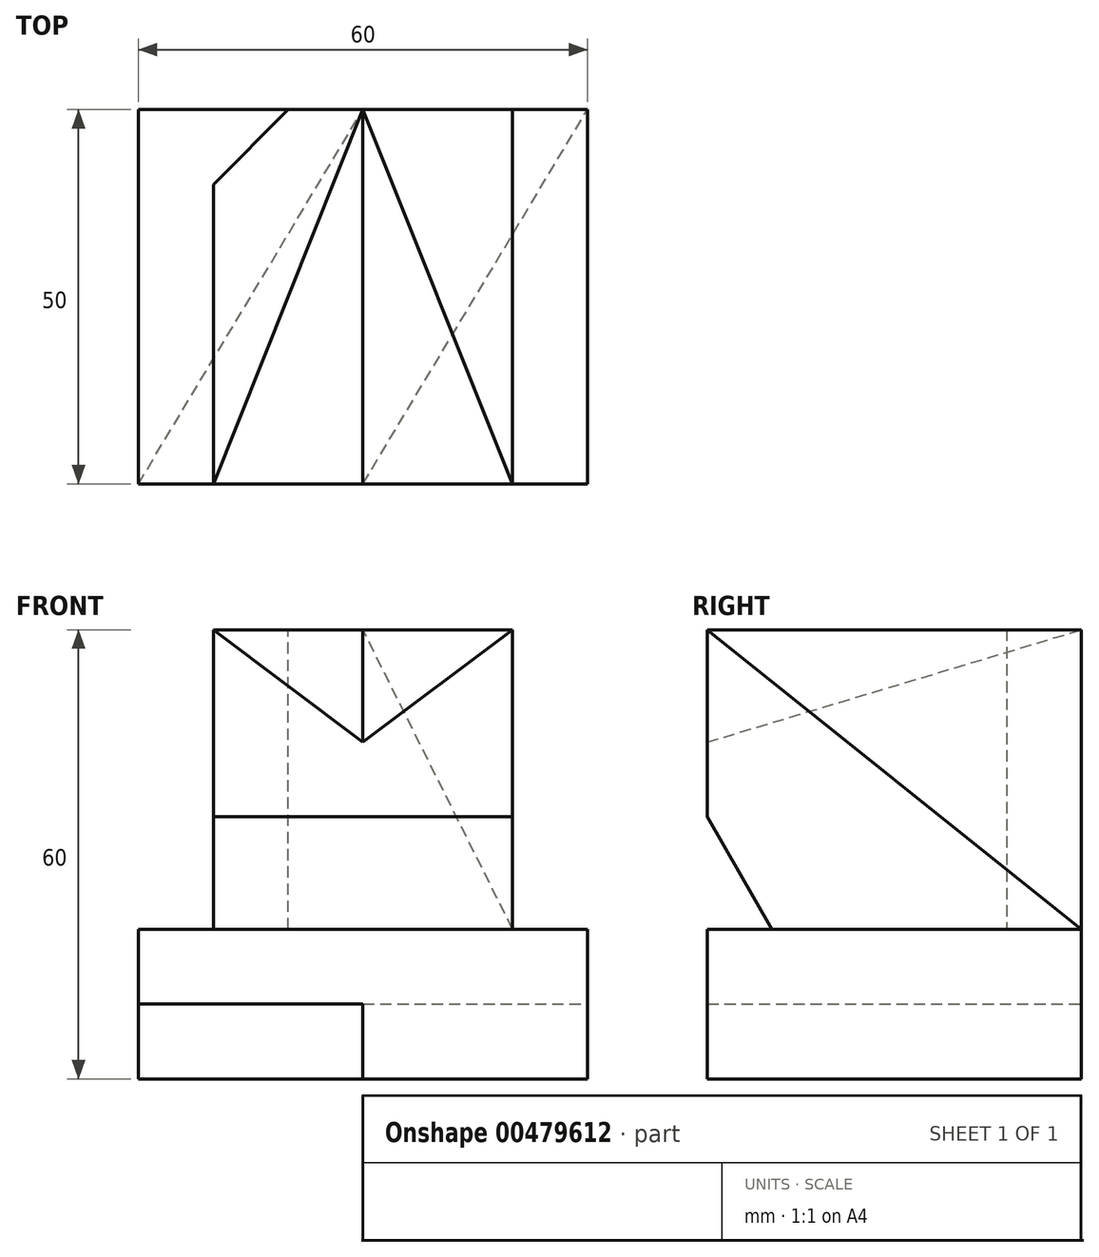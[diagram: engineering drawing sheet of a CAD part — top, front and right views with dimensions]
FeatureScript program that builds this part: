
annotation { "Feature Type Name" : "Feature", "Feature Type Description" : "" }
export const myFeature = defineFeature(function(context is Context, id is Id, definition is map)
    precondition{}
    {
        {
            var Q0;
            Q0=qCreatedBy(makeId("Top.planeOp"),FACE);
            var sketch = newSketch(context, id + "F0", { "sketchPlane" : qUnion([Q0])});
            skLineSegment(sketch, "E0.bottom", {"start": v(0, 0) * mm, "end": v(60, 0) * mm});
            skLineSegment(sketch, "E0.top", {"start": v(0, 50) * mm, "end": v(60, 50) * mm});
            skLineSegment(sketch, "E0.left", {"start": v(0, 0) * mm, "end": v(0, 50) * mm});
            skLineSegment(sketch, "E0.right", {"start": v(60, 0) * mm, "end": v(60, 50) * mm});
            skSolve(sketch);
        }
        {
            var Q0;
            Q0 = qSketchRegion(id + "F0", true);
            extrude(context, id + "F1", {"entities" : qUnion([Q0]), "depth" : 60 * mm});
        }
        {
            var Q0;
            Q0=makeQuery(id+"F1.opExtrude","SWEPT_FACE",FACE,{"disambiguationData":[OSD([sQuery(id+"F0.wireOp",EDGE,"E0.bottom")])]});
            var sketch = newSketch(context, id + "F2", { "sketchPlane" : qUnion([Q0])});
            skLineSegment(sketch, "E1.bottom", {"start": v(0, 60) * mm, "end": v(10, 60) * mm});
            skLineSegment(sketch, "E1.top", {"start": v(0, 20) * mm, "end": v(10, 20) * mm});
            skLineSegment(sketch, "E1.left", {"start": v(0, 60) * mm, "end": v(0, 20) * mm});
            skLineSegment(sketch, "E1.right", {"start": v(10, 60) * mm, "end": v(10, 20) * mm});
            skSolve(sketch);
        }
        {
            var Q0;
            Q0=makeQuery(id+"F2.imprint","IMPRINT",FACE,{"disambiguationData":[TD([[makeQuery(id+"F2.imprint","IMPRINT",EDGE,{"derivedFrom":sQuery(id+"F2.wireOp",EDGE,"E1.bottom")}),-1.0]])]});
            extrude(context, id + "F3", {"entities" : qUnion([Q0]), "operationType" : NewBodyOperationType.REMOVE, "endBound" : BoundingType.THROUGH_ALL, "oppositeDirection" : true, "depth" : 25 * mm, "offsetDistance" : 25 * mm});
        }
        {
            var Q0;
            Q0=makeQuery(id+"F1.opExtrude","SWEPT_FACE",FACE,{"disambiguationData":[OSD([sQuery(id+"F0.wireOp",EDGE,"E0.bottom")])]});
            var sketch = newSketch(context, id + "F4", { "sketchPlane" : qUnion([Q0])});
            skLineSegment(sketch, "E2.bottom", {"start": v(60, 60) * mm, "end": v(50, 60) * mm});
            skLineSegment(sketch, "E2.top", {"start": v(60, 20) * mm, "end": v(50, 20) * mm});
            skLineSegment(sketch, "E2.left", {"start": v(60, 60) * mm, "end": v(60, 20) * mm});
            skLineSegment(sketch, "E2.right", {"start": v(50, 60) * mm, "end": v(50, 20) * mm});
            skSolve(sketch);
        }
        {
            var Q0;
            Q0=makeQuery(id+"F4.imprint","IMPRINT",FACE,{"disambiguationData":[TD([[makeQuery(id+"F4.imprint","IMPRINT",EDGE,{"derivedFrom":sQuery(id+"F4.wireOp",EDGE,"E2.bottom")}),-1.0]])]});
            extrude(context, id + "F5", {"entities" : qUnion([Q0]), "operationType" : NewBodyOperationType.REMOVE, "endBound" : BoundingType.THROUGH_ALL, "oppositeDirection" : true, "depth" : 25 * mm, "offsetDistance" : 25 * mm});
        }
        {
            var Q0;
            Q0=makeQuery(id+"F1.opExtrude","CAP_FACE",FACE,{"disambiguationData":[OSD([sQuery(id+"F0.wireOp",EDGE,"E0.bottom"),sQuery(id+"F0.wireOp",EDGE,"E0.top"),sQuery(id+"F0.wireOp",EDGE,"E0.left"),sQuery(id+"F0.wireOp",EDGE,"E0.right")])],"isStart":true});
            var sketch = newSketch(context, id + "F6", { "sketchPlane" : qUnion([Q0])});
            skLineSegment(sketch, "E3", {"start": v(0, 0) * mm, "end": v(30, -50) * mm});
            skLineSegment(sketch, "E4", {"start": v(30, 0) * mm, "end": v(60, -50) * mm});
            skSolve(sketch);
        }
        {
            var Q0;
            {var subQ0=sQuery(id+"F6.wireOp",EDGE,"E3");Q0=makeQuery(id+"F6.imprint","IMPRINT",FACE,{"disambiguationData":[TD([[makeQuery(id+"F6.imprint","IMPRINT",EDGE,{"derivedFrom":subQ0}),1.0]])]});}
            extrude(context, id + "F7", {"entities" : qUnion([Q0]), "operationType" : NewBodyOperationType.REMOVE, "oppositeDirection" : true, "depth" : 10 * mm, "offsetDistance" : 25 * mm});
        }
        {
            var Q0;
            Q0=makeQuery(id+"F3.boolean.opBoolean","INTERSECT",EDGE,{"derivedFrom":[makeQuery(id+"F1.opExtrude","SWEPT_FACE",FACE,{"disambiguationData":[OSD([sQuery(id+"F0.wireOp",EDGE,"E0.top")])]}),makeQuery(id+"F3.opExtrude","SWEPT_FACE",FACE,{"disambiguationData":[OSD([sQuery(id+"F2.wireOp",EDGE,"E1.right")])]})]});
            chamfer(context, id + "F8", {"entities" : qUnion([Q0]), "width" : 10 * mm, "tangentPropagation" : true});
        }
        {
            var Q0;
            Q0=makeQuery(id+"F5.boolean.opBoolean","COPY",FACE,{"derivedFrom":makeQuery(id+"F5.opExtrude","SWEPT_FACE",FACE,{"disambiguationData":[OSD([sQuery(id+"F4.wireOp",EDGE,"E2.right")])]})});
            var sketch = newSketch(context, id + "F9", { "sketchPlane" : qUnion([Q0])});
            skLineSegment(sketch, "E5", {"start": v(0, 35) * mm, "end": v(8.66, 20) * mm});
            skSolve(sketch);
        }
        {
            var Q0;
            {var subQ0=sQuery(id+"F9.wireOp",EDGE,"E5");Q0=makeQuery(id+"F9.imprint","IMPRINT",FACE,{"disambiguationData":[TD([[makeQuery(id+"F9.imprint","IMPRINT",EDGE,{"derivedFrom":subQ0}),-1.0]])]});}
            extrude(context, id + "F10", {"entities" : qUnion([Q0]), "operationType" : NewBodyOperationType.REMOVE, "endBound" : BoundingType.THROUGH_ALL, "oppositeDirection" : true, "depth" : 25 * mm, "offsetDistance" : 25 * mm});
        }
        {
            var Q0;
            {var subQ0=sQuery(id+"F0.wireOp",EDGE,"E0.bottom");Q0=makeQuery(id+"F10.boolean.opBoolean","SPLIT",FACE,{"disambiguationData":[TD([makeQuery(id+"F3.boolean.opBoolean","COPY",FACE,{"derivedFrom":makeQuery(id+"F3.opExtrude","SWEPT_FACE",FACE,{"disambiguationData":[OSD([sQuery(id+"F2.wireOp",EDGE,"E1.right")])]})})])],"derivedFrom":makeQuery(id+"F1.opExtrude","SWEPT_FACE",FACE,{"disambiguationData":[OSD([subQ0])]})});}
            var sketch = newSketch(context, id + "F11", { "sketchPlane" : qUnion([Q0])});
            skLineSegment(sketch, "E6", {"start": v(10, 60) * mm, "end": v(30, 45) * mm});
            skPoint(sketch, "E6.endSnap0", {"position": v(10, 45) * mm});
            skLineSegment(sketch, "E7", {"start": v(30, 45) * mm, "end": v(50, 60) * mm});
            skSolve(sketch);
        }
        {
            var Q0;
            Q0=makeQuery(id+"F5.boolean.opBoolean","COPY",FACE,{"derivedFrom":makeQuery(id+"F5.opExtrude","SWEPT_FACE",FACE,{"disambiguationData":[OSD([sQuery(id+"F4.wireOp",EDGE,"E2.right")])]})});
            var sketch = newSketch(context, id + "F12", { "sketchPlane" : qUnion([Q0])});
            skLineSegment(sketch, "E8", {"start": v(50, 60) * mm, "end": v(0, 45) * mm});
            skSolve(sketch);
        }
        {
            var Q0;
            Q0=makeQuery(id+"F11.imprint","IMPRINT",FACE,{"disambiguationData":[TD([[makeQuery(id+"F11.imprint","IMPRINT",EDGE,{"derivedFrom":sQuery(id+"F11.wireOp",EDGE,"E6")}),1.0]])]});
            var Q1;
            Q1=sQuery(id+"F12.wireOp",EDGE,"E8");
            sweep(context, id + "F13", {"operationType" : NewBodyOperationType.REMOVE, "profiles" : qUnion([Q0]), "path" : qUnion([Q1])});
        }
        {
            var Q0;
            Q0=makeQuery(id+"F5.boolean.opBoolean","COPY",FACE,{"derivedFrom":makeQuery(id+"F5.opExtrude","SWEPT_FACE",FACE,{"disambiguationData":[OSD([sQuery(id+"F4.wireOp",EDGE,"E2.right")])]})});
            var sketch = newSketch(context, id + "F14", { "sketchPlane" : qUnion([Q0])});
            skLineSegment(sketch, "E9", {"start": v(0, 60) * mm, "end": v(50, 20) * mm});
            skSolve(sketch);
        }
        {
            var Q0;
            {var subQ1=sQuery(id+"F0.wireOp",EDGE,"E0.top");var subQ2=sQuery(id+"F0.wireOp",EDGE,"E0.bottom");var subQ3=makeQuery(id+"F1.opExtrude","CAP_FACE",FACE,{"disambiguationData":[OSD([subQ2,subQ1,sQuery(id+"F0.wireOp",EDGE,"E0.left"),sQuery(id+"F0.wireOp",EDGE,"E0.right")])],"isStart":false});Q0=makeQuery(id+"F13.boolean.opBoolean","SPLIT",FACE,{"disambiguationData":[TD([makeQuery(id+"F5.boolean.opBoolean","COPY",FACE,{"derivedFrom":makeQuery(id+"F5.opExtrude","SWEPT_FACE",FACE,{"disambiguationData":[OSD([sQuery(id+"F4.wireOp",EDGE,"E2.right")])]})})])],"derivedFrom":subQ3});}
            var Q1;
            Q1=sQuery(id+"F14.wireOp",EDGE,"E9");
            sweep(context, id + "F15", {"operationType" : NewBodyOperationType.REMOVE, "profiles" : qUnion([Q0]), "path" : qUnion([Q1])});
        }
    });
